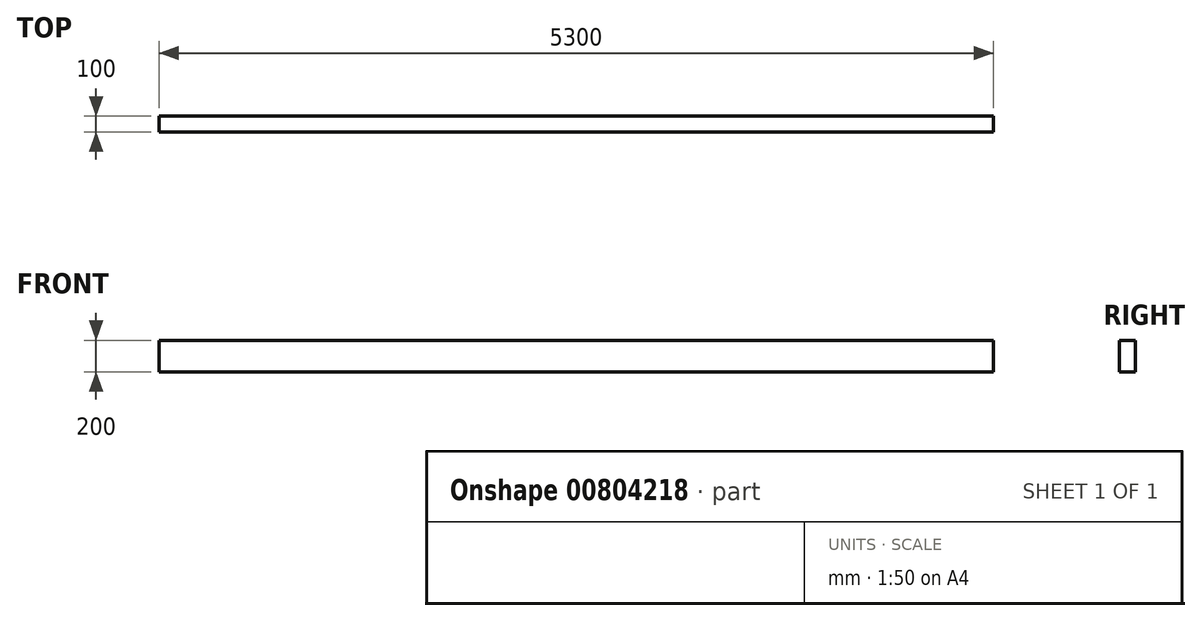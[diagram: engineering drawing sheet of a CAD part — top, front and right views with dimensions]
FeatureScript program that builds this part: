
annotation { "Feature Type Name" : "Feature", "Feature Type Description" : "" }
export const myFeature = defineFeature(function(context is Context, id is Id, definition is map)
    precondition{}
    {
        {
            var Q0;
            Q0=qCreatedBy(makeId("Front.planeOp"),FACE);
            var sketch = newSketch(context, id + "F0", { "sketchPlane" : qUnion([Q0])});
            skLineSegment(sketch, "E0.bottom", {"start": v(0, 0) * mm, "end": v(5300, 0) * mm});
            skLineSegment(sketch, "E0.top", {"start": v(0, -200) * mm, "end": v(5300, -200) * mm});
            skLineSegment(sketch, "E0.left", {"start": v(0, 0) * mm, "end": v(0, -200) * mm});
            skLineSegment(sketch, "E0.right", {"start": v(5300, 0) * mm, "end": v(5300, -200) * mm});
            skSolve(sketch);
        }
        {
            var Q0;
            Q0=makeQuery(id+"F0.imprint","IMPRINT",FACE,{"disambiguationData":[TD([[makeQuery(id+"F0.imprint","IMPRINT",EDGE,{"derivedFrom":sQuery(id+"F0.wireOp",EDGE,"E0.bottom")}),-1.0]])]});
            extrude(context, id + "F1", {"entities" : qUnion([Q0]), "depth" : 100 * mm, "offsetDistance" : 25 * mm});
        }
    });
